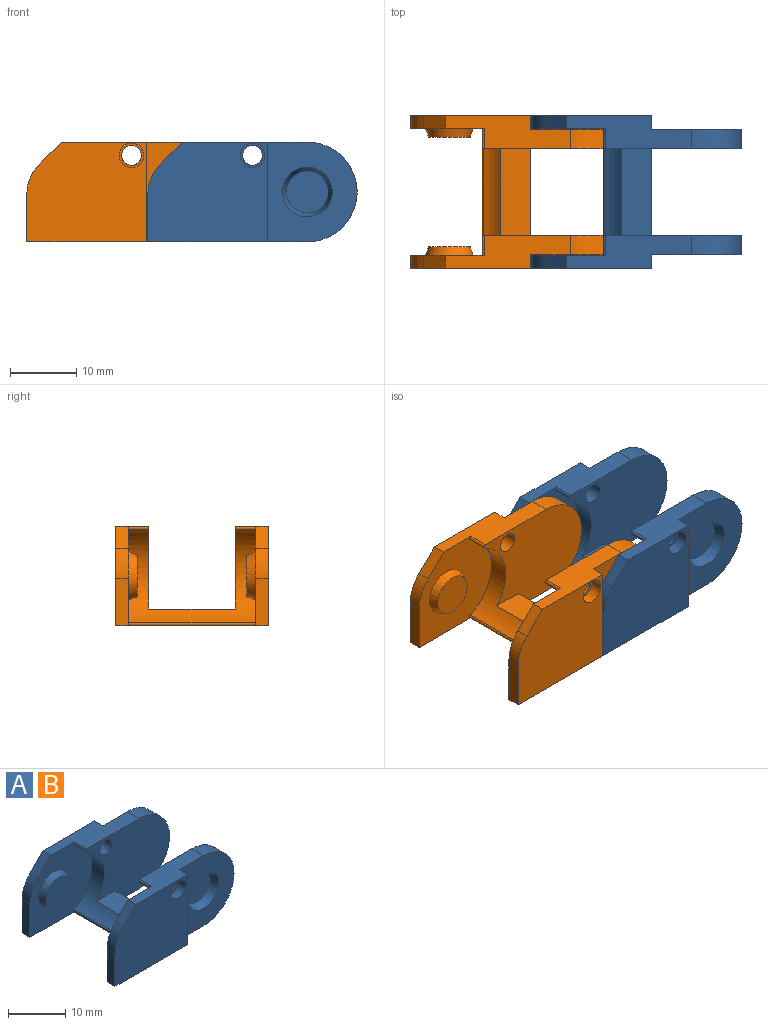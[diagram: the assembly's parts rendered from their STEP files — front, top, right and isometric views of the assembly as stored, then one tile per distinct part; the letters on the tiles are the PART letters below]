
ASSEMBLY  parts=2 mates=1
PART A: 45 faces, bbox 31.5x23x15 mm
  f0: cylinder r=1.5mm len=3.2mm, axis (0,1,0), area 30.2mm2, adj f5,f44
  f1: plane 18x15mm, normal (0,1,0), area 243.6mm2, adj f2,f22,f23,f25,f26,f27,f37,f38
  f2: plane 24x23mm, normal (0,0,-1), area 238.9mm2, adj f1,f4,f5,f6,f7,f11,f12,f14
  f3: plane 18.8x5mm, normal (0,0,1), area 63.9mm2, adj f5,f6,f7,f8,f11,f15,f16,f17
  f4: plane 7.11x1.95mm, normal (-1,0,0), area 13.9mm2, adj f2,f7,f9,f16
  f5: plane 20.78x15mm, normal (0,1,0), area 218.4mm2, adj f0,f2,f3,f10,f11,f12,f13,f15
  f6: plane 15x2.05mm, normal (1,0,0), area 30.7mm2, adj f2,f3,f7,f17
  f7: plane 18x15mm, normal (0,-1,0), area 244.8mm2, adj f2,f3,f4,f6,f8,f9,f43
  f8: plane 3.3x3.3mm, normal (-0.71,0,0.71), area 9.1mm2, adj f3,f7,f9,f16
  f9: cylinder r=6.5mm len=4.6mm, axis (0,-1,0), area 10mm2, adj f4,f7,f8,f16
  f10: cylinder r=7.6mm len=19.1mm, axis (0,-1,0), area 148.7mm2, adj f5,f13,f14,f15,f16,f24,f29,f30
  f11: cylinder r=7.5mm len=15mm, axis (0,-1,0), area 69.5mm2, adj f2,f3,f5,f17
  f12: plane 13x2.5mm, normal (1,0,0), area 32.5mm2, adj f2,f5,f13,f24
  f13: plane 13x4.51mm, normal (0,0,1), area 58.6mm2, adj f5,f10,f12,f24
  f14: cylinder r=0.3mm len=19.1mm, axis (0,-1,0), area 15.6mm2, adj f2,f10,f16,f30
  f15: cylinder r=0.3mm len=3.05mm, axis (0,-1,0), area 2.5mm2, adj f3,f5,f10,f16
  f16: plane 15.37x15mm, normal (0,1,0), area 152.8mm2, adj f2,f3,f4,f8,f9,f10,f14,f15
  f17: plane 15x13.5mm, normal (0,-1,0), area 134.2mm2, adj f2,f3,f6,f11,f18
  f18: cone r=3.75mm half-angle=20deg, axis (0,-1,0), area 37mm2, adj f17,f19
  f19: plane 6.34x6.34mm, normal (0,-1,0), area 31.5mm2, adj f18
  f20: cone r=3.6mm half-angle=20deg, axis (0,-1,0), area 29.2mm2, adj f16,f21
  f21: plane 6.25x6.25mm, normal (0,1,0), area 30.7mm2, adj f20
  f22: plane 18.8x5mm, normal (0,0,1), area 63.9mm2, adj f1,f24,f25,f26,f28,f29,f30,f31
  f23: plane 7.11x1.95mm, normal (-1,0,0), area 13.9mm2, adj f1,f2,f27,f30
  f24: plane 20.78x15mm, normal (0,-1,0), area 218.4mm2, adj f2,f10,f12,f13,f22,f28,f29,f36
  f25: plane 15x2.05mm, normal (1,0,0), area 30.7mm2, adj f1,f2,f22,f31
  f26: plane 3.3x3.3mm, normal (-0.71,0,0.71), area 9.1mm2, adj f1,f22,f27,f30
  f27: cylinder r=6.5mm len=4.6mm, axis (0,1,0), area 10mm2, adj f1,f23,f26,f30
  f28: cylinder r=7.5mm len=15mm, axis (0,1,0), area 69.5mm2, adj f2,f22,f24,f31
  f29: cylinder r=0.3mm len=3.05mm, axis (0,1,0), area 2.5mm2, adj f10,f22,f24,f30
  f30: plane 15.37x15mm, normal (0,-1,0), area 152.8mm2, adj f2,f10,f14,f22,f23,f26,f27,f29
  f31: plane 15x13.5mm, normal (0,1,0), area 134.2mm2, adj f2,f22,f25,f28,f32
  f32: cone r=3.75mm half-angle=20deg, axis (0,1,0), area 37mm2, adj f31,f33
  f33: plane 6.34x6.34mm, normal (0,1,0), area 31.5mm2, adj f32
  f34: cone r=3.6mm half-angle=20deg, axis (0,1,0), area 29.2mm2, adj f30,f35
  f35: plane 6.25x6.25mm, normal (0,-1,0), area 30.7mm2, adj f34
  f36: cylinder r=1.5mm len=3.2mm, axis (0,1,0), area 30.2mm2, adj f24,f40,f42
  f37: plane 4x1.8mm, normal (0,0,-1), area 7.2mm2, adj f1,f39,f40,f41,f42
  f38: plane 4x1.8mm, normal (0,0,1), area 7.2mm2, adj f1,f39,f40,f41,f42
  f39: plane 3x1.8mm, normal (1,0,0), area 5.4mm2, adj f1,f37,f38,f40
  f40: plane 3x2mm, normal (0,1,0), area 2.5mm2, adj f36,f37,f38,f39
  f41: plane 3x1.8mm, normal (-1,0,0), area 5.4mm2, adj f1,f37,f38,f42
  f42: plane 3x2mm, normal (0,1,0), area 2.5mm2, adj f36,f37,f38,f41
  f43: cylinder r=1.85mm len=3.7mm, axis (0,-1,0), area 20.9mm2, adj f7,f44
  f44: plane 3.7x3.7mm, normal (0,-1,0), area 3.7mm2, adj f0,f43
PART B: same geometry as A
PLACE A rot(axis=(0,1,0),0deg) t=(2.78,-0.31,4.79)mm
PLACE B t=(-15.42,-0.31,4.79)mm
MATE cylindrical A.f20 <-> B.f11  axis (0,-1,0) through (8.58,19.44,12.29)mm
